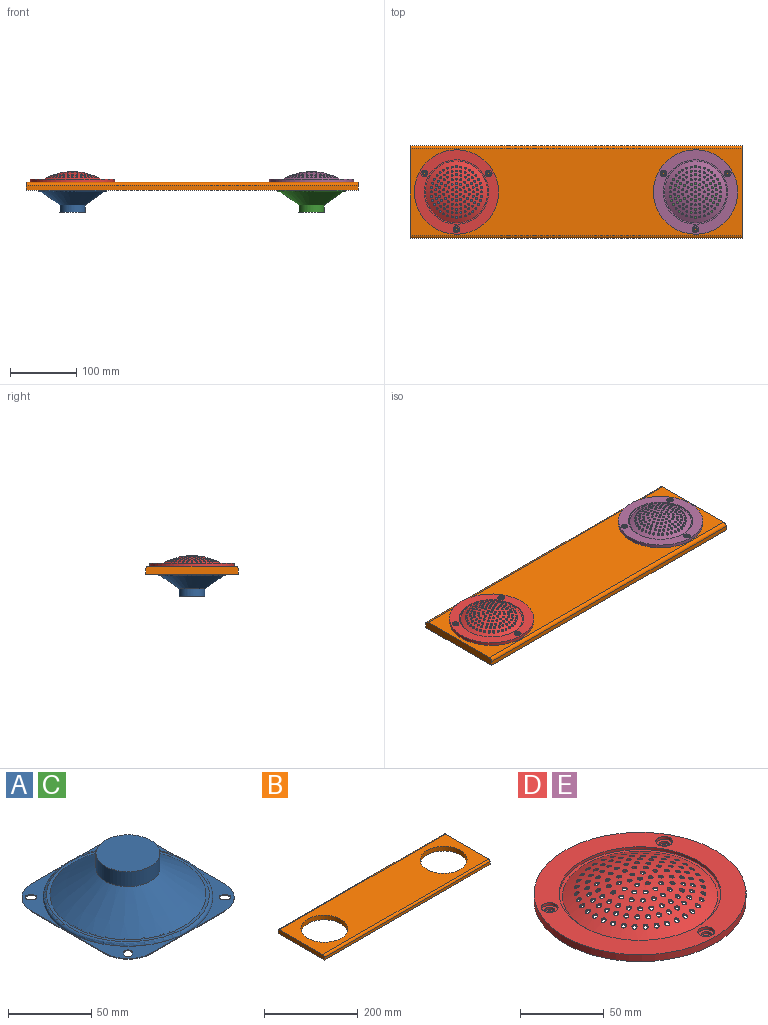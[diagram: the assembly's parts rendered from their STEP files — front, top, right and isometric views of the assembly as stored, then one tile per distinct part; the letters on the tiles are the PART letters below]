
ASSEMBLY  parts=5 mates=4
PART A: 42 faces, bbox 110.4x110.4x33.9 mm
  f0: plane 51x51mm, normal (0,0,1), area 442.7mm2, adj f3,f4,f16,f17,f18,f25,f27,f37
  f1: plane 51x51mm, normal (0,0,1), area 442.7mm2, adj f4,f5,f6,f19,f20,f21,f26,f37
  f2: plane 51x51mm, normal (0,0,1), area 442.7mm2, adj f6,f7,f8,f10,f11,f12,f22,f37
  f3: cylinder r=20mm len=20mm, axis (0,0,-1), area 15.7mm2, adj f0,f4,f27,f29
  f4: plane 62x0.5mm, normal (0,1,0), area 31mm2, adj f0,f1,f3,f5,f29
  f5: cylinder r=20mm len=20mm, axis (0,0,-1), area 15.7mm2, adj f1,f4,f6,f29
  f6: plane 62x0.5mm, normal (-1,0,0), area 31mm2, adj f1,f2,f5,f7,f29
  f7: cylinder r=20mm len=20mm, axis (0,0,-1), area 15.7mm2, adj f2,f6,f8,f29
  f8: plane 62x0.5mm, normal (0,-1,0), area 31mm2, adj f2,f7,f9,f28,f29
  f9: cylinder r=20mm len=20mm, axis (0,0,-1), area 15.7mm2, adj f8,f27,f28,f29
  f10: plane 1.41x1.41mm, normal (0.71,-0.71,0), area 1mm2, adj f2,f11,f22,f29
  f11: cylinder r=2.5mm len=4.27mm, axis (0,0,-1), area 3.9mm2, adj f2,f10,f12,f29
  f12: plane 1.41x1.41mm, normal (-0.71,0.71,0), area 1mm2, adj f2,f11,f22,f29
  f13: plane 1.41x1.41mm, normal (0.71,0.71,0), area 1mm2, adj f14,f24,f28,f29
  f14: cylinder r=2.5mm len=4.27mm, axis (0,0,-1), area 3.9mm2, adj f13,f15,f28,f29
  f15: plane 1.41x1.41mm, normal (-0.71,-0.71,0), area 1mm2, adj f14,f24,f28,f29
  f16: plane 1.41x1.41mm, normal (-0.71,0.71,0), area 1mm2, adj f0,f17,f25,f29
  f17: cylinder r=2.5mm len=4.27mm, axis (0,0,-1), area 3.9mm2, adj f0,f16,f18,f29
  f18: plane 1.41x1.41mm, normal (0.71,-0.71,0), area 1mm2, adj f0,f17,f25,f29
  f19: cylinder r=2.5mm len=4.27mm, axis (0,0,-1), area 3.9mm2, adj f1,f20,f26,f29
  f20: plane 1.41x1.41mm, normal (-0.71,-0.71,0), area 1mm2, adj f1,f19,f21,f29
  f21: cylinder r=2.5mm len=4.27mm, axis (0,0,-1), area 3.9mm2, adj f1,f20,f26,f29
  f22: cylinder r=2.5mm len=4.27mm, axis (0,0,-1), area 3.9mm2, adj f2,f10,f12,f29
  f23: cylinder r=50.5mm len=101mm, axis (0,0,-1), area 158.7mm2, adj f29,f31
  f24: cylinder r=2.5mm len=4.27mm, axis (0,0,-1), area 3.9mm2, adj f13,f15,f28,f29
  f25: cylinder r=2.5mm len=4.27mm, axis (0,0,-1), area 3.9mm2, adj f0,f16,f18,f29
  f26: plane 1.41x1.41mm, normal (0.71,0.71,0), area 1mm2, adj f1,f19,f21,f29
  f27: plane 62x0.5mm, normal (1,0,0), area 31mm2, adj f0,f3,f9,f28,f29
  f28: plane 51x51mm, normal (0,0,1), area 442.7mm2, adj f8,f9,f13,f14,f15,f24,f27,f37
  f29: plane 102x102mm, normal (0,0,-1), area 1930.3mm2, adj f3,f4,f5,f6,f7,f8,f9,f10
  f30: plane 98x98mm, normal (0,0,1), area 603.2mm2, adj f36,f37
  f31: plane 101x101mm, normal (0,0,-1), area 430.2mm2, adj f23,f32
  f32: sphere r=112.21mm, area 7316.5mm2, adj f31,f33
  f33: sphere r=38.23mm, area 691.3mm2, adj f32
  f34: plane 38.54x38.54mm, normal (0,0,1), area 1166.5mm2, adj f35
  f35: cylinder r=19.27mm len=38.54mm, axis (0,0,1), area 1331.8mm2, adj f34,f36
  f36: cone r=19.27mm half-angle=54.9deg, axis (0,0,-1), area 7057.8mm2, adj f30,f35
  f37: torus R=49mm, axis (0,0,-1), area 992.4mm2, adj f0,f1,f2,f28,f30
  f38: plane 36.8x36.8mm, normal (0,0,-1), area 1063.6mm2, adj f39
  f39: cone r=18.4mm half-angle=54.9deg, axis (0,0,-1), area 6872.6mm2, adj f38,f41
  f40: sphere r=112.71mm, area 6957.9mm2, adj f41
  f41: plane 92.26x92.26mm, normal (0,0,1), area 30.8mm2, adj f39,f40
PART B: 10 faces, bbox 500x140x12 mm
  f0: plane 500x7mm, normal (0,1,0), area 3500mm2, adj f1,f3,f5,f7
  f1: plane 140x12mm, normal (-1,0,0), area 1669.3mm2, adj f0,f2,f4,f5,f6,f7
  f2: plane 500x7mm, normal (0,-1,0), area 3500mm2, adj f1,f3,f5,f6
  f3: plane 140x12mm, normal (1,0,0), area 1669.3mm2, adj f0,f2,f4,f5,f6,f7
  f4: plane 500x130mm, normal (0,0,1), area 49292mm2, adj f1,f3,f6,f7,f8,f9
  f5: plane 500x140mm, normal (0,0,-1), area 54292mm2, adj f0,f1,f2,f3,f8,f9
  f6: cylinder r=5mm len=500mm, axis (-1,0,0), area 3927mm2, adj f1,f2,f3,f4
  f7: cylinder r=5mm len=500mm, axis (1,0,0), area 3927mm2, adj f0,f1,f3,f4
  f8: cylinder r=50mm len=100mm, axis (0,0,1), area 3769.9mm2, adj f4,f5
  f9: cylinder r=50mm len=100mm, axis (0,0,1), area 3769.9mm2, adj f4,f5
PART C: same geometry as A
PART D: 150 faces, bbox 127x127x16 mm
  f0: cylinder r=3mm len=6mm, axis (0,0,1), area 28.3mm2, adj f141,f149
  f1: cylinder r=3mm len=6mm, axis (0,0,1), area 28.3mm2, adj f142,f147
  f2: cylinder r=3mm len=6mm, axis (0,0,1), area 28.3mm2, adj f143,f145
  f3: cylinder r=1.5mm len=3mm, axis (0,0,1), area 14.1mm2, adj f10,f143
  f4: cylinder r=1.5mm len=3mm, axis (0,0,1), area 14.1mm2, adj f10,f142
  f5: cylinder r=1.5mm len=3mm, axis (0,0,1), area 14.1mm2, adj f10,f141
  f6: sphere r=88.66mm, area 6388mm2, adj f11,f14,f15,f16,f17,f18,f19,f20
  f7: sphere r=89.66mm, area 6361.9mm2, adj f12,f14,f15,f16,f17,f18,f19,f20
  f8: plane 127x127mm, normal (0,0,1), area 5042.3mm2, adj f9,f13,f144,f146,f148
  f9: cylinder r=63.5mm len=127mm, axis (0,0,1), area 1994.9mm2, adj f8,f10
  f10: plane 127x127mm, normal (0,0,-1), area 5853.6mm2, adj f3,f4,f5,f9,f11
  f11: cylinder r=46.5mm len=93mm, axis (0,0,1), area 534.1mm2, adj f6,f10
  f12: plane 97x97mm, normal (0,0,1), area 596.9mm2, adj f7,f13
  f13: cylinder r=48.5mm len=97mm, axis (0,0,1), area 609.5mm2, adj f8,f12
  f14: cylinder r=1.5mm len=3mm, axis (0,0,-1), area 9.4mm2, adj f6,f7
  f15: cylinder r=1.5mm len=3mm, axis (0,0,-1), area 10.4mm2, adj f6,f7
  f16: cylinder r=1.5mm len=3mm, axis (0,0,-1), area 10.4mm2, adj f6,f7
  f17: cylinder r=1.5mm len=3mm, axis (0,0,-1), area 10.4mm2, adj f6,f7
  f18: cylinder r=1.5mm len=3mm, axis (0,0,-1), area 10.4mm2, adj f6,f7
  f19: cylinder r=1.5mm len=3mm, axis (0,0,-1), area 10.4mm2, adj f6,f7
  f20: cylinder r=1.5mm len=3mm, axis (0,0,-1), area 10.4mm2, adj f6,f7
  f21: cylinder r=1.5mm len=3mm, axis (0,0,-1), area 9.9mm2, adj f6,f7
  f22: cylinder r=1.5mm len=3mm, axis (0,0,-1), area 9.9mm2, adj f6,f7
  f23: cylinder r=1.5mm len=3mm, axis (0,0,-1), area 9.9mm2, adj f6,f7
  f24: cylinder r=1.5mm len=3mm, axis (0,0,-1), area 9.9mm2, adj f6,f7
  f25: cylinder r=1.5mm len=3mm, axis (0,0,-1), area 9.9mm2, adj f6,f7
  f26: cylinder r=1.5mm len=3mm, axis (0,0,-1), area 9.9mm2, adj f6,f7
  f27: cylinder r=1.5mm len=3mm, axis (0,0,-1), area 9.9mm2, adj f6,f7
  f28: cylinder r=1.5mm len=3mm, axis (0,0,-1), area 9.9mm2, adj f6,f7
  f29: cylinder r=1.5mm len=3mm, axis (0,0,-1), area 9.9mm2, adj f6,f7
  f30: cylinder r=1.5mm len=3mm, axis (0,0,-1), area 9.9mm2, adj f6,f7
  f31: cylinder r=1.5mm len=3mm, axis (0,0,-1), area 9.9mm2, adj f6,f7
  f32: cylinder r=1.5mm len=3mm, axis (0,0,-1), area 9.9mm2, adj f6,f7
  f33: cylinder r=1.5mm len=3mm, axis (0,0,-1), area 9.9mm2, adj f6,f7
  f34: cylinder r=1.5mm len=3mm, axis (0,0,-1), area 9.9mm2, adj f6,f7
  f35: cylinder r=1.5mm len=3mm, axis (0,0,-1), area 9.9mm2, adj f6,f7
  f36: cylinder r=1.5mm len=3mm, axis (0,0,-1), area 9.9mm2, adj f6,f7
  f37: cylinder r=1.5mm len=3mm, axis (0,0,-1), area 9.9mm2, adj f6,f7
  f38: cylinder r=1.5mm len=3mm, axis (0,0,-1), area 9.9mm2, adj f6,f7
  f39: cylinder r=1.5mm len=3mm, axis (0,0,-1), area 9.9mm2, adj f6,f7
  f40: cylinder r=1.5mm len=3mm, axis (0,0,-1), area 9.9mm2, adj f6,f7
  f41: cylinder r=1.5mm len=3mm, axis (0,0,-1), area 9.9mm2, adj f6,f7
  f42: cylinder r=1.5mm len=3mm, axis (0,0,-1), area 9.9mm2, adj f6,f7
  f43: cylinder r=1.5mm len=3mm, axis (0,0,-1), area 9.9mm2, adj f6,f7
  f44: cylinder r=1.5mm len=3mm, axis (0,0,-1), area 10.1mm2, adj f6,f7
  f45: cylinder r=1.5mm len=3mm, axis (0,0,-1), area 10.1mm2, adj f6,f7
  f46: cylinder r=1.5mm len=3mm, axis (0,0,-1), area 10.1mm2, adj f6,f7
  f47: cylinder r=1.5mm len=3mm, axis (0,0,-1), area 10.4mm2, adj f6,f7
  f48: cylinder r=1.5mm len=3mm, axis (0,0,-1), area 10.4mm2, adj f6,f7
  f49: cylinder r=1.5mm len=3mm, axis (0,0,-1), area 10.4mm2, adj f6,f7
  f50: cylinder r=1.5mm len=3mm, axis (0,0,-1), area 10.4mm2, adj f6,f7
  f51: cylinder r=1.5mm len=3mm, axis (0,0,-1), area 10.4mm2, adj f6,f7
  f52: cylinder r=1.5mm len=3mm, axis (0,0,-1), area 10.4mm2, adj f6,f7
  f53: cylinder r=1.5mm len=3mm, axis (0,0,-1), area 10.4mm2, adj f6,f7
  f54: cylinder r=1.5mm len=3mm, axis (0,0,-1), area 10.4mm2, adj f6,f7
  f55: cylinder r=1.5mm len=3mm, axis (0,0,-1), area 10.4mm2, adj f6,f7
  f56: cylinder r=1.5mm len=3mm, axis (0,0,-1), area 10.4mm2, adj f6,f7
  f57: cylinder r=1.5mm len=3mm, axis (0,0,-1), area 10.4mm2, adj f6,f7
  f58: cylinder r=1.5mm len=3mm, axis (0,0,-1), area 10.4mm2, adj f6,f7
  f59: cylinder r=1.5mm len=3mm, axis (0,0,-1), area 10.4mm2, adj f6,f7
  f60: cylinder r=1.5mm len=3mm, axis (0,0,-1), area 10.4mm2, adj f6,f7
  f61: cylinder r=1.5mm len=3mm, axis (0,0,-1), area 10.4mm2, adj f6,f7
  f62: cylinder r=1.5mm len=3mm, axis (0,0,-1), area 10.4mm2, adj f6,f7
  f63: cylinder r=1.5mm len=3mm, axis (0,0,-1), area 10.4mm2, adj f6,f7
  f64: cylinder r=1.5mm len=3mm, axis (0,0,-1), area 10.4mm2, adj f6,f7
  f65: cylinder r=1.5mm len=3mm, axis (0,0,-1), area 10.4mm2, adj f6,f7
  f66: cylinder r=1.5mm len=3mm, axis (0,0,-1), area 10.4mm2, adj f6,f7
  f67: cylinder r=1.5mm len=3mm, axis (0,0,-1), area 10.4mm2, adj f6,f7
  f68: cylinder r=1.5mm len=3mm, axis (0,0,-1), area 10.4mm2, adj f6,f7
  f69: cylinder r=1.5mm len=3mm, axis (0,0,-1), area 10.4mm2, adj f6,f7
  f70: cylinder r=1.5mm len=3mm, axis (0,0,-1), area 10.4mm2, adj f6,f7
  f71: cylinder r=1.5mm len=3mm, axis (0,0,-1), area 10.4mm2, adj f6,f7
  f72: cylinder r=1.5mm len=3mm, axis (0,0,-1), area 10.4mm2, adj f6,f7
  f73: cylinder r=1.5mm len=3mm, axis (0,0,-1), area 10.4mm2, adj f6,f7
  f74: cylinder r=1.5mm len=3mm, axis (0,0,-1), area 10.4mm2, adj f6,f7
  f75: cylinder r=1.5mm len=3mm, axis (0,0,-1), area 10.4mm2, adj f6,f7
  f76: cylinder r=1.5mm len=3mm, axis (0,0,-1), area 10.4mm2, adj f6,f7
  f77: cylinder r=1.5mm len=3mm, axis (0,0,-1), area 9.5mm2, adj f6,f7
  f78: cylinder r=1.5mm len=3mm, axis (0,0,-1), area 9.5mm2, adj f6,f7
  f79: cylinder r=1.5mm len=3mm, axis (0,0,-1), area 9.5mm2, adj f6,f7
  f80: cylinder r=1.5mm len=3mm, axis (0,0,-1), area 9.5mm2, adj f6,f7
  f81: cylinder r=1.5mm len=3mm, axis (0,0,-1), area 9.5mm2, adj f6,f7
  f82: cylinder r=1.5mm len=3mm, axis (0,0,-1), area 9.7mm2, adj f6,f7
  f83: cylinder r=1.5mm len=3mm, axis (0,0,-1), area 9.1mm2, adj f6,f7
  f84: cylinder r=1.5mm len=3mm, axis (0,0,-1), area 9.7mm2, adj f6,f7
  f85: cylinder r=1.5mm len=3mm, axis (0,0,-1), area 9.7mm2, adj f6,f7
  f86: cylinder r=1.5mm len=3mm, axis (0,0,-1), area 9.7mm2, adj f6,f7
  f87: cylinder r=1.5mm len=3mm, axis (0,0,-1), area 9.7mm2, adj f6,f7
  f88: cylinder r=1.5mm len=3mm, axis (0,0,-1), area 9.7mm2, adj f6,f7
  f89: cylinder r=1.5mm len=3mm, axis (0,0,-1), area 9.7mm2, adj f6,f7
  f90: cylinder r=1.5mm len=3mm, axis (0,0,-1), area 9.7mm2, adj f6,f7
  f91: cylinder r=1.5mm len=3mm, axis (0,0,-1), area 9.7mm2, adj f6,f7
  f92: cylinder r=1.5mm len=3mm, axis (0,0,-1), area 9.7mm2, adj f6,f7
  f93: cylinder r=1.5mm len=3mm, axis (0,0,-1), area 9.7mm2, adj f6,f7
  f94: cylinder r=1.5mm len=3mm, axis (0,0,-1), area 9.5mm2, adj f6,f7
  f95: cylinder r=1.5mm len=3mm, axis (0,0,-1), area 6.5mm2, adj f6,f7
  f96: cylinder r=1.5mm len=3mm, axis (0,0,-1), area 9.5mm2, adj f6,f7
  f97: cylinder r=1.5mm len=3mm, axis (0,0,-1), area 9.5mm2, adj f6,f7
  f98: cylinder r=1.5mm len=3mm, axis (0,0,-1), area 9.5mm2, adj f6,f7
  f99: cylinder r=1.5mm len=3mm, axis (0,0,-1), area 9.5mm2, adj f6,f7
  f100: cylinder r=1.5mm len=3mm, axis (0,0,-1), area 9.5mm2, adj f6,f7
  f101: cylinder r=1.5mm len=3mm, axis (0,0,-1), area 9.9mm2, adj f6,f7
  f102: cylinder r=1.5mm len=3mm, axis (0,0,-1), area 10.1mm2, adj f6,f7
  f103: cylinder r=1.5mm len=3mm, axis (0,0,-1), area 9.5mm2, adj f6,f7
  f104: cylinder r=1.5mm len=3mm, axis (0,0,-1), area 9.5mm2, adj f6,f7
  f105: cylinder r=1.5mm len=3mm, axis (0,0,-1), area 9.5mm2, adj f6,f7
  f106: cylinder r=1.5mm len=3mm, axis (0,0,-1), area 9.5mm2, adj f6,f7
  f107: cylinder r=1.5mm len=3mm, axis (0,0,-1), area 9.5mm2, adj f6,f7
  f108: cylinder r=1.5mm len=3mm, axis (0,0,-1), area 9.5mm2, adj f6,f7
  f109: cylinder r=1.5mm len=3mm, axis (0,0,-1), area 10.1mm2, adj f6,f7
  f110: cylinder r=1.5mm len=3mm, axis (0,0,-1), area 10.1mm2, adj f6,f7
  f111: cylinder r=1.5mm len=3mm, axis (0,0,-1), area 10.1mm2, adj f6,f7
  f112: cylinder r=1.5mm len=3mm, axis (0,0,-1), area 10.1mm2, adj f6,f7
  f113: cylinder r=1.5mm len=3mm, axis (0,0,-1), area 10.1mm2, adj f6,f7
  f114: cylinder r=1.5mm len=3mm, axis (0,0,-1), area 10.1mm2, adj f6,f7
  f115: cylinder r=1.5mm len=3mm, axis (0,0,-1), area 10.1mm2, adj f6,f7
  f116: cylinder r=1.5mm len=3mm, axis (0,0,-1), area 10.1mm2, adj f6,f7
  f117: cylinder r=1.5mm len=3mm, axis (0,0,-1), area 10.1mm2, adj f6,f7
  f118: cylinder r=1.5mm len=3mm, axis (0,0,-1), area 10.1mm2, adj f6,f7
  f119: cylinder r=1.5mm len=3mm, axis (0,0,-1), area 10.1mm2, adj f6,f7
  f120: cylinder r=1.5mm len=3mm, axis (0,0,-1), area 10.1mm2, adj f6,f7
  f121: cylinder r=1.5mm len=3mm, axis (0,0,-1), area 10.1mm2, adj f6,f7
  f122: cylinder r=1.5mm len=3mm, axis (0,0,-1), area 10.1mm2, adj f6,f7
  f123: cylinder r=1.5mm len=3mm, axis (0,0,-1), area 10.1mm2, adj f6,f7
  f124: cylinder r=1.5mm len=3mm, axis (0,0,-1), area 10.1mm2, adj f6,f7
  f125: cylinder r=1.5mm len=3mm, axis (0,0,-1), area 10.1mm2, adj f6,f7
  f126: cylinder r=1.5mm len=3mm, axis (0,0,-1), area 10.1mm2, adj f6,f7
  f127: cylinder r=1.5mm len=3mm, axis (0,0,-1), area 10.1mm2, adj f6,f7
  f128: cylinder r=1.5mm len=3mm, axis (0,0,-1), area 10.1mm2, adj f6,f7
  f129: cylinder r=1.5mm len=3mm, axis (0,0,-1), area 10.1mm2, adj f6,f7
  f130: cylinder r=1.5mm len=3mm, axis (0,0,-1), area 10.1mm2, adj f6,f7
  f131: cylinder r=1.5mm len=3mm, axis (0,0,-1), area 10.1mm2, adj f6,f7
  f132: cylinder r=1.5mm len=3mm, axis (0,0,-1), area 10.1mm2, adj f6,f7
  f133: cylinder r=1.5mm len=3mm, axis (0,0,-1), area 10.1mm2, adj f6,f7
  f134: cylinder r=1.5mm len=3mm, axis (0,0,-1), area 10.1mm2, adj f6,f7
  f135: cylinder r=1.5mm len=3mm, axis (0,0,-1), area 9.7mm2, adj f6,f7
  f136: cylinder r=1.5mm len=3mm, axis (0,0,-1), area 9.7mm2, adj f6,f7
  f137: cylinder r=1.5mm len=3mm, axis (0,0,-1), area 9.7mm2, adj f6,f7
  f138: cylinder r=1.5mm len=3mm, axis (0,0,-1), area 9.7mm2, adj f6,f7
  f139: cylinder r=1.5mm len=3mm, axis (0,0,-1), area 9.7mm2, adj f6,f7
  f140: cylinder r=1.5mm len=3mm, axis (0,0,-1), area 9.7mm2, adj f6,f7
  f141: plane 6x6mm, normal (0,0,1), area 21.2mm2, adj f0,f5
  f142: plane 6x6mm, normal (0,0,1), area 21.2mm2, adj f1,f4
  f143: plane 6x6mm, normal (0,0,1), area 21.2mm2, adj f2,f3
  f144: cylinder r=5mm len=10mm, axis (0,0,1), area 62.8mm2, adj f8,f145
  f145: plane 10x10mm, normal (0,0,1), area 50.3mm2, adj f2,f144
  f146: cylinder r=5mm len=10mm, axis (0,0,1), area 62.8mm2, adj f8,f147
  f147: plane 10x10mm, normal (0,0,1), area 50.3mm2, adj f1,f146
  f148: cylinder r=5mm len=10mm, axis (0,0,1), area 62.8mm2, adj f8,f149
  f149: plane 10x10mm, normal (0,0,1), area 50.3mm2, adj f0,f148
PART E: same geometry as D
PLACE A rot(axis=(1,0,0),180deg) t=(-151.26,43.15,31.84)mm
PLACE B t=(28.74,43.15,31.84)mm
PLACE C rot(axis=(1,0,0),180deg) t=(208.74,43.15,31.84)mm
PLACE D t=(-151.26,43.15,43.84)mm
PLACE E t=(208.74,43.15,43.84)mm
MATE fastened C.f23 <-> B.f8  axis (0,0,1) through (208.74,43.15,31.84)mm
MATE fastened A.f23 <-> B.f9  axis (0,0,1) through (-151.26,43.15,31.84)mm
MATE fastened E.f9 <-> B.f8  axis (0,0,-1) through (208.74,43.15,43.84)mm
MATE fastened D.f9 <-> B.f9  axis (0,0,-1) through (-151.26,43.15,43.84)mm
